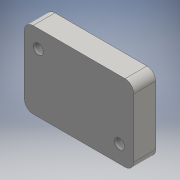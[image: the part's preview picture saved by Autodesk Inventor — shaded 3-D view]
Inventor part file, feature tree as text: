
AUTODESK INVENTOR PART (.ipt)
format: ipt  version: 2016 (Build 200138000, 138)  size: 128,000 bytes
history: native  units: mm
features: sketch x3, extrude x2, fillet x2, hole x1
ambient origin geometry x8: Origin, YZ Plane, XZ Plane, XY Plane, X Axis, Y Axis, Z Axis, Center Point
bodies: Solid1 (feature_tree)
feature tree (8):
  extrude  "Extrusion1"  Depth=35.0mm
  extrude  "Extrusion2"  Depth=10.0mm
  hole  "Hole1"  [1 undecoded]
  fillet  "Fillet1"  Radius=5.0mm
  fillet  "Fillet2"  Radius=6.5mm
  sketch  "Sketch1"  dims[d0=50.0mm d1=35.0mm]
  sketch  "Sketch2"  dims[d2=10.0mm d3=0.0mm d4=22.5mm]
  sketch  "Sketch3"  dims[d5=17.5mm d6=25.0mm d7=5.0mm d8=0.0mm d9=6.5mm d10=8.0mm d11=6.5mm d12=8.0mm d13=4.5mm d14=6.0mm d15=8.5mm d16=4.0mm d17=90.0deg d18=20.0mm d19=20.594885mm d20=4.0mm d21=4.0mm]
note: 1 required parameter value undecoded (feature->parameter linkage not recoverable at this tier; creation-order binding heuristic only, values carry confidence <= 0.55)
